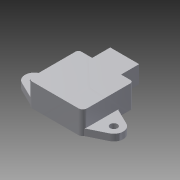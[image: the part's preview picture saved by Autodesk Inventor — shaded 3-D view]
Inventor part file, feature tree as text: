
AUTODESK INVENTOR PART (.ipt)
format: ipt  version: 2015 (Build 190159000, 159)  size: 206,848 bytes
history: native  units: mm
features: extrude x7, sketch x5, chamfer x2, projected_geometry x1
ambient origin geometry x8: Origin, YZ Plane, XZ Plane, XY Plane, X Axis, Y Axis, Z Axis, Center Point
bodies: Solid1 (feature_tree)
feature tree (15):
  sketch  "Sketch1"  dims[d0=38.0mm d1=35.0mm]
  extrude  "Extrusion1"  Depth=35.0mm
  extrude  "Extrusion2"  Depth=2.0mm
  extrude  "Extrusion3"  Depth=13.0mm
  chamfer  "Chamfer1"  Distance=13.0mm
  sketch  "Sketch3"  dims[d4=3.0mm d5=13.0mm]
  extrude  "Extrusion4"  Depth=0.5mm
  extrude  "Extrusion5"  Depth=2.0mm
  extrude  "Extrusion6"  Depth=0.5mm
  chamfer  "Chamfer3"  Distance=4.537856mm
  extrude  "Extrusion7"  Depth=13.0mm
  sketch  "Sketch2"  dims[d2=55.0mm d3=2.0mm]
  projected_geometry  "Projected Loop1"
  sketch  "Sketch4"  dims[d6=4.5mm]
  sketch  "Sketch5"  dims[d7=5.0mm d8=13.0mm d9=4.363323mm d12=2.0mm d13=4.537856mm d14=4.537856mm d15=13.0mm d16=4.537856mm d17=4.537856mm d18=2.0mm d19=4.6mm d20=0.0mm d21=16.0mm d22=0.0mm d24=16.0mm d25=15.1mm d26=2.0mm d27=0.0mm d28=0.5mm d29=2.0mm d30=45.0deg d31=8.0mm d32=2.0mm d33=2.0mm d34=12.0mm d35=0.0mm d39=9.7mm d40=20.0mm d41=13.0mm d42=0.0mm d43=8.0mm d44=6.0mm d45=0.0mm d46=1.0mm d47=1.99mm d48=45.0deg d49=0.5mm d50=0.0mm]
